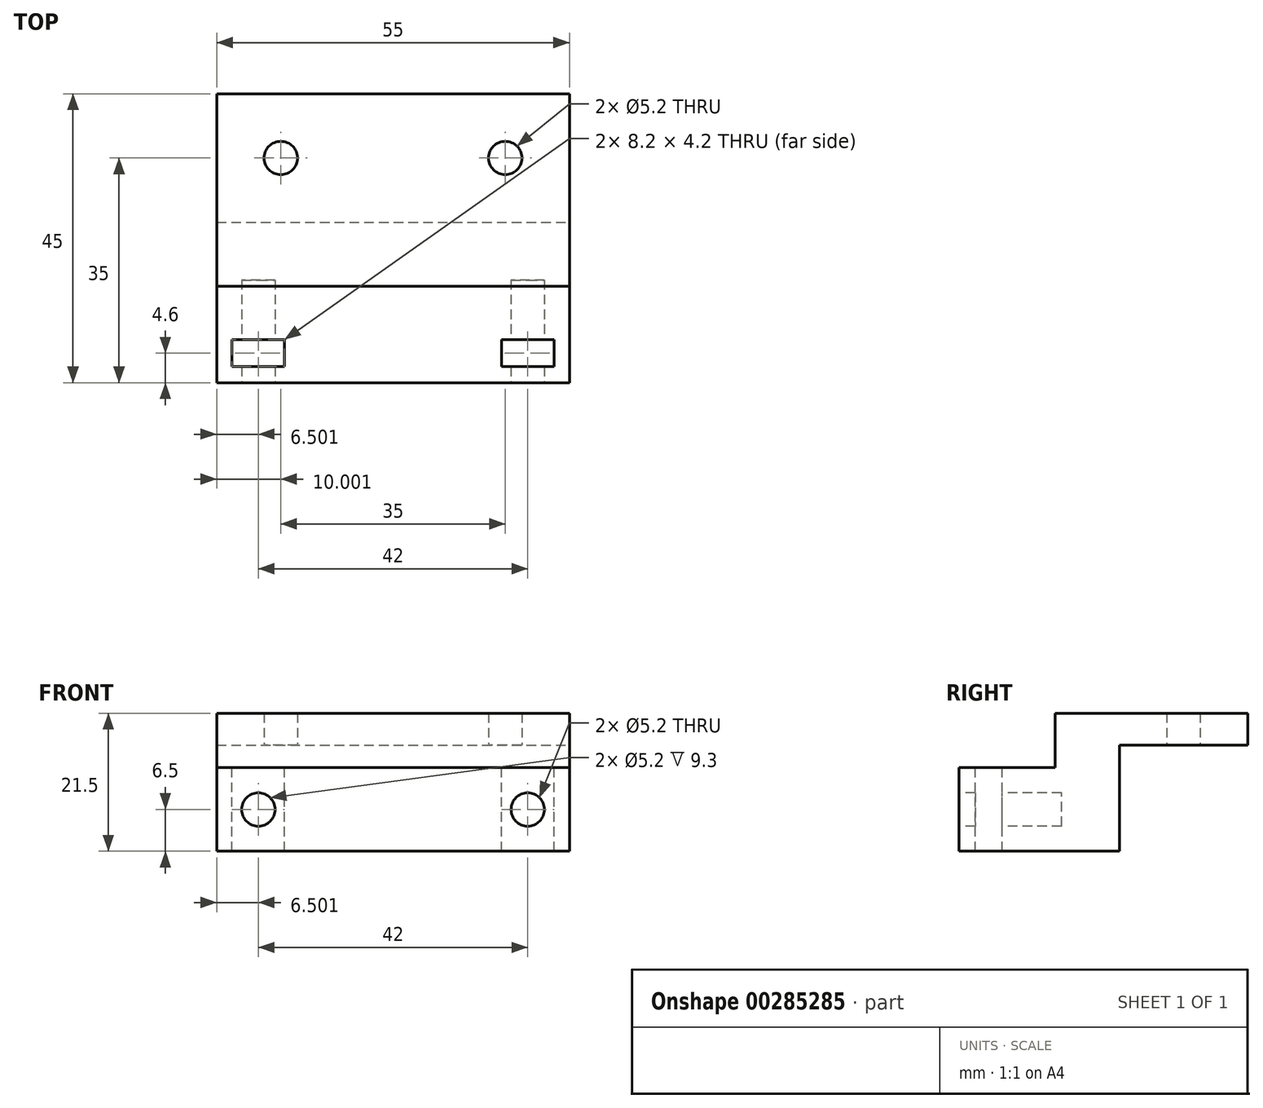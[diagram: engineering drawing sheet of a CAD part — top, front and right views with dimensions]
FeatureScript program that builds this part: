
annotation { "Feature Type Name" : "Feature", "Feature Type Description" : "" }
export const myFeature = defineFeature(function(context is Context, id is Id, definition is map)
    precondition{}
    {
        {
            var Q0;
            Q0=qCreatedBy(makeId("Top.planeOp"),FACE);
            var sketch = newSketch(context, id + "F0", { "sketchPlane" : qUnion([Q0])});
            skLineSegment(sketch, "E0.bottom", {"start": v(-8.43, 11.65) * mm, "end": v(46.57, 11.65) * mm});
            skLineSegment(sketch, "E0.top", {"start": v(-8.43, -13.35) * mm, "end": v(46.57, -13.35) * mm});
            skLineSegment(sketch, "E0.left", {"start": v(-8.43, 11.65) * mm, "end": v(-8.43, -13.35) * mm});
            skLineSegment(sketch, "E0.right", {"start": v(46.57, 11.65) * mm, "end": v(46.57, -13.35) * mm});
            skSolve(sketch);
        }
        {
            var Q0;
            Q0 = qSketchRegion(id + "F0", true);
            extrude(context, id + "F1", {"entities" : qUnion([Q0]), "depth" : 13 * mm});
        }
        {
            var Q0;
            Q0=makeQuery(id+"F1.opExtrude","SWEPT_FACE",FACE,{"disambiguationData":[OSD([sQuery(id+"F0.wireOp",EDGE,"E0.top")])]});
            var sketch = newSketch(context, id + "F2", { "sketchPlane" : qUnion([Q0])});
            skLineSegment(sketch, "E1.bottom", {"start": v(-8.43, 13) * mm, "end": v(-1.93, 13) * mm});
            skLineSegment(sketch, "E1.top", {"start": v(-8.43, 6.5) * mm, "end": v(-1.93, 6.5) * mm});
            skLineSegment(sketch, "E1.left", {"start": v(-8.43, 13) * mm, "end": v(-8.43, 6.5) * mm});
            skLineSegment(sketch, "E1.right", {"start": v(-1.93, 13) * mm, "end": v(-1.93, 6.5) * mm});
            skLineSegment(sketch, "E2.bottom", {"start": v(46.57, 13) * mm, "end": v(40.07, 13) * mm});
            skLineSegment(sketch, "E2.top", {"start": v(46.57, 6.5) * mm, "end": v(40.07, 6.5) * mm});
            skLineSegment(sketch, "E2.left", {"start": v(46.57, 13) * mm, "end": v(46.57, 6.5) * mm});
            skLineSegment(sketch, "E2.right", {"start": v(40.07, 13) * mm, "end": v(40.07, 6.5) * mm});
            skCircle(sketch, "E3", {"center": v(-1.93, 6.5) * mm, "radius": 2.6 * mm});
            skCircle(sketch, "E4", {"center": v(40.07, 6.5) * mm, "radius": 2.6 * mm});
            skSolve(sketch);
        }
        {
            var Q0;
            {var subQ0=sQuery(id+"F2.wireOp",EDGE,"E1.right");var subQ1=sQuery(id+"F2.wireOp",EDGE,"E1.top");var subQ2=makeQuery(id+"F2.imprint","INTERSECT",VERTEX,{"derivedFrom":[subQ1,subQ0]});Q0=makeQuery(id+"F2.imprint","IMPRINT",FACE,{"disambiguationData":[TD([[makeQuery(id+"F2.imprint","IMPRINT",EDGE,{"disambiguationData":[TD([[subQ2,1.0]])],"derivedFrom":subQ1}),1.0]])]});}
            var Q1;
            {var subQ0=sQuery(id+"F2.wireOp",EDGE,"E1.right");var subQ1=sQuery(id+"F2.wireOp",EDGE,"E1.top");var subQ2=makeQuery(id+"F2.imprint","INTERSECT",VERTEX,{"derivedFrom":[subQ1,subQ0]});Q1=makeQuery(id+"F2.imprint","IMPRINT",FACE,{"disambiguationData":[TD([[makeQuery(id+"F2.imprint","IMPRINT",EDGE,{"disambiguationData":[TD([[subQ2,1.0]])],"derivedFrom":subQ1}),-1.0]])]});}
            var Q2;
            {var subQ0=sQuery(id+"F2.wireOp",EDGE,"E2.right");var subQ1=sQuery(id+"F2.wireOp",EDGE,"E2.top");var subQ2=makeQuery(id+"F2.imprint","INTERSECT",VERTEX,{"derivedFrom":[subQ1,subQ0]});Q2=makeQuery(id+"F2.imprint","IMPRINT",FACE,{"disambiguationData":[TD([[makeQuery(id+"F2.imprint","IMPRINT",EDGE,{"disambiguationData":[TD([[subQ2,1.0]])],"derivedFrom":subQ1}),-1.0]])]});}
            var Q3;
            {var subQ0=sQuery(id+"F2.wireOp",EDGE,"E2.right");var subQ1=sQuery(id+"F2.wireOp",EDGE,"E2.top");var subQ2=makeQuery(id+"F2.imprint","INTERSECT",VERTEX,{"derivedFrom":[subQ1,subQ0]});Q3=makeQuery(id+"F2.imprint","IMPRINT",FACE,{"disambiguationData":[TD([[makeQuery(id+"F2.imprint","IMPRINT",EDGE,{"disambiguationData":[TD([[subQ2,1.0]])],"derivedFrom":subQ1}),1.0]])]});}
            extrude(context, id + "F3", {"entities" : qUnion([Q0, Q1, Q2, Q3]), "operationType" : NewBodyOperationType.REMOVE, "oppositeDirection" : true, "depth" : 16 * mm});
        }
        {
            var Q0;
            Q0=makeQuery(id+"F1.opExtrude","CAP_FACE",FACE,{"disambiguationData":[OSD([sQuery(id+"F0.wireOp",EDGE,"E0.bottom"),sQuery(id+"F0.wireOp",EDGE,"E0.top"),sQuery(id+"F0.wireOp",EDGE,"E0.left"),sQuery(id+"F0.wireOp",EDGE,"E0.right")])],"isStart":false});
            var sketch = newSketch(context, id + "F4", { "sketchPlane" : qUnion([Q0])});
            skLineSegment(sketch, "E5.bottom", {"start": v(-8.43, -13.35) * mm, "end": v(-1.93, -13.35) * mm});
            skLineSegment(sketch, "E5.top", {"start": v(-8.43, -10.85) * mm, "end": v(-1.93, -10.85) * mm});
            skLineSegment(sketch, "E5.left", {"start": v(-8.43, -13.35) * mm, "end": v(-8.43, -10.85) * mm});
            skLineSegment(sketch, "E5.right", {"start": v(-1.93, -13.35) * mm, "end": v(-1.93, -10.85) * mm});
            skLineSegment(sketch, "E6.bottom", {"start": v(-1.93, -10.85) * mm, "end": v(2.17, -10.85) * mm});
            skLineSegment(sketch, "E6.top", {"start": v(-1.93, -6.65) * mm, "end": v(2.17, -6.65) * mm});
            skLineSegment(sketch, "E6.left", {"start": v(-1.93, -10.85) * mm, "end": v(-1.93, -6.65) * mm});
            skLineSegment(sketch, "E6.right", {"start": v(2.17, -10.85) * mm, "end": v(2.17, -6.65) * mm});
            skLineSegment(sketch, "E7.bottom", {"start": v(-1.93, -6.65) * mm, "end": v(-6.03, -6.65) * mm});
            skLineSegment(sketch, "E7.top", {"start": v(-1.93, -10.85) * mm, "end": v(-6.03, -10.85) * mm});
            skLineSegment(sketch, "E7.left", {"start": v(-1.93, -6.65) * mm, "end": v(-1.93, -10.85) * mm});
            skLineSegment(sketch, "E7.right", {"start": v(-6.03, -6.65) * mm, "end": v(-6.03, -10.85) * mm});
            skLineSegment(sketch, "E8", {"start": v(-8.43, 11.65) * mm, "end": v(46.57, 11.65) * mm});
            skLineSegment(sketch, "E9", {"start": v(46.57, 11.65) * mm, "end": v(19.07, 11.65) * mm});
            skLineSegment(sketch, "E10", {"start": v(19.07, 11.65) * mm, "end": v(19.07, -13.35) * mm});
            skLineSegment(sketch, "E11.MirrorCS", {"start": v(35.97, -10.85) * mm, "end": v(35.97, -6.65) * mm});
            skLineSegment(sketch, "E12.MirrorCS", {"start": v(44.17, -6.65) * mm, "end": v(44.17, -10.85) * mm});
            skLineSegment(sketch, "E13.MirrorCS", {"start": v(40.07, -6.65) * mm, "end": v(44.17, -6.65) * mm});
            skLineSegment(sketch, "E14.MirrorCS", {"start": v(40.07, -10.85) * mm, "end": v(44.17, -10.85) * mm});
            skLineSegment(sketch, "E15.MirrorCS", {"start": v(40.07, -6.65) * mm, "end": v(35.97, -6.65) * mm});
            skLineSegment(sketch, "E16.MirrorCS", {"start": v(40.07, -10.85) * mm, "end": v(35.97, -10.85) * mm});
            skSolve(sketch);
        }
        {
            var Q0;
            Q0=makeQuery(id+"F4.imprint","IMPRINT",FACE,{"disambiguationData":[TD([[makeQuery(id+"F4.imprint","IMPRINT",EDGE,{"derivedFrom":sQuery(id+"F4.wireOp",EDGE,"E11.MirrorCS")}),-1.0]])]});
            var Q1;
            Q1=makeQuery(id+"F4.imprint","IMPRINT",FACE,{"disambiguationData":[TD([[makeQuery(id+"F4.imprint","IMPRINT",EDGE,{"derivedFrom":sQuery(id+"F4.wireOp",EDGE,"E6.bottom")}),1.0]])]});
            var Q2;
            Q2=makeQuery(id+"F4.imprint","IMPRINT",FACE,{"disambiguationData":[TD([[makeQuery(id+"F4.imprint","IMPRINT",EDGE,{"derivedFrom":sQuery(id+"F4.wireOp",EDGE,"E7.bottom")}),1.0]])]});
            extrude(context, id + "F5", {"entities" : qUnion([Q0, Q1, Q2]), "operationType" : NewBodyOperationType.REMOVE, "oppositeDirection" : true, "depth" : 31.6 * mm});
        }
        {
            var Q0;
            Q0=makeQuery(id+"F1.opExtrude","CAP_FACE",FACE,{"disambiguationData":[OSD([sQuery(id+"F0.wireOp",EDGE,"E0.bottom"),sQuery(id+"F0.wireOp",EDGE,"E0.top"),sQuery(id+"F0.wireOp",EDGE,"E0.left"),sQuery(id+"F0.wireOp",EDGE,"E0.right")])],"isStart":false});
            var sketch = newSketch(context, id + "F6", { "sketchPlane" : qUnion([Q0])});
            skLineSegment(sketch, "E17.bottom", {"start": v(-8.43, 11.65) * mm, "end": v(46.57, 11.65) * mm});
            skLineSegment(sketch, "E17.top", {"start": v(-8.43, 1.65) * mm, "end": v(46.57, 1.65) * mm});
            skLineSegment(sketch, "E17.left", {"start": v(-8.43, 11.65) * mm, "end": v(-8.43, 1.65) * mm});
            skLineSegment(sketch, "E17.right", {"start": v(46.57, 11.65) * mm, "end": v(46.57, 1.65) * mm});
            skLineSegment(sketch, "E18.bottom", {"start": v(46.57, 11.65) * mm, "end": v(-8.43, 11.65) * mm});
            skLineSegment(sketch, "E18.top", {"start": v(46.57, 31.65) * mm, "end": v(-8.43, 31.65) * mm});
            skLineSegment(sketch, "E18.left", {"start": v(46.57, 11.65) * mm, "end": v(46.57, 31.65) * mm});
            skLineSegment(sketch, "E18.right", {"start": v(-8.43, 11.65) * mm, "end": v(-8.43, 31.65) * mm});
            skLineSegment(sketch, "E19", {"start": v(46.57, 21.65) * mm, "end": v(-8.43, 21.65) * mm});
            skCircle(sketch, "E20", {"center": v(36.57, 21.65) * mm, "radius": 2.6 * mm});
            skCircle(sketch, "E21", {"center": v(1.57, 21.65) * mm, "radius": 2.6 * mm});
            skSolve(sketch);
        }
        {
            var Q0;
            Q0 = qSketchRegion(id + "F6", true);
            extrude(context, id + "F7", {"entities" : qUnion([Q0]), "operationType" : NewBodyOperationType.ADD, "depth" : 5 * mm});
        }
        {
            var Q0;
            Q0=makeQuery(id+"F7.opExtrude","CAP_FACE",FACE,{"disambiguationData":[OSD([sQuery(id+"F6.wireOp",EDGE,"E17.top"),sQuery(id+"F6.wireOp",EDGE,"E17.left"),sQuery(id+"F6.wireOp",EDGE,"E17.right"),sQuery(id+"F6.wireOp",EDGE,"E18.top"),sQuery(id+"F6.wireOp",EDGE,"E18.left"),sQuery(id+"F6.wireOp",EDGE,"E18.right"),sQuery(id+"F6.wireOp",EDGE,"E20"),sQuery(id+"F6.wireOp",EDGE,"E21")])],"isStart":false});
            extrude(context, id + "F8", {"entities" : qUnion([Q0]), "operationType" : NewBodyOperationType.ADD, "depth" : 3.5 * mm});
        }
        {
            var Q0;
            Q0=makeQuery(id+"F7.opExtrude","CAP_FACE",FACE,{"disambiguationData":[OSD([sQuery(id+"F6.wireOp",EDGE,"E17.top"),sQuery(id+"F6.wireOp",EDGE,"E17.left"),sQuery(id+"F6.wireOp",EDGE,"E17.right"),sQuery(id+"F6.wireOp",EDGE,"E18.top"),sQuery(id+"F6.wireOp",EDGE,"E18.left"),sQuery(id+"F6.wireOp",EDGE,"E18.right"),sQuery(id+"F6.wireOp",EDGE,"E20"),sQuery(id+"F6.wireOp",EDGE,"E21")])],"isStart":true});
            extrude(context, id + "F9", {"entities" : qUnion([Q0]), "operationType" : NewBodyOperationType.REMOVE, "oppositeDirection" : true, "depth" : 3.5 * mm});
        }
    });
